# Revit family: WS920
name_source: partatom
category: Lighting Fixtures
units: mm (PartAtom-declared; Revit-internal decimal feet)

## family parameters
Cut with Voids When Loaded = No
Host = Face
Light Source = Yes
Maintain Annotation Orientation = No
Part Type = Normal
Room Calculation Point = No
Round Connector Dimension = Use Diameter
Shared = No

## types (4) — shared parameters
Color Filter = 16777215
Default Elevation = 1219 mm
Description = WALL SCONCE
Dimming Lamp Color Temperature Shift = <None>
Light Source Symbol Size = 610 mm
URL = https://cdn.shopify.com

## per-type parameters (varying)
| type | Height |
| WS920-1 | 457 mm |
| WS920-2 | 610 mm |
| WS920-4 | 1219 mm |
| WS920-5 | 1524 mm  [stored 5 ft] |

note: column(s) folded — value = type name in every type: Model

note: [stored X ft] marks values corroborated as IEEE doubles in the binary element streams (Revit-internal decimal feet)

## geometry (parser evidence)
native form markers: Sweep x2
no freeform markers — native parametric forms only
